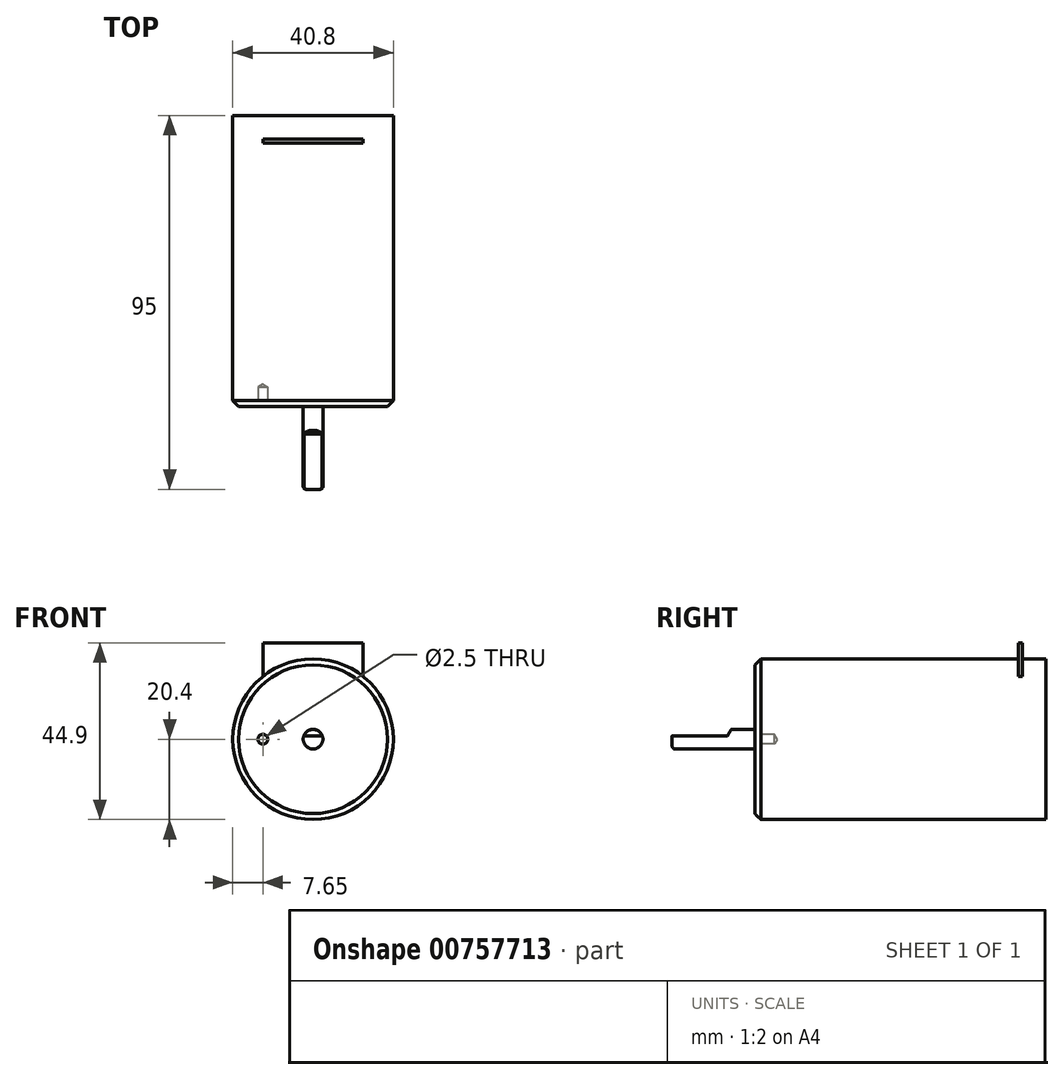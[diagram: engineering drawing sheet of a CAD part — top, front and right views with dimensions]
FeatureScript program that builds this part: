
annotation { "Feature Type Name" : "Feature", "Feature Type Description" : "" }
export const myFeature = defineFeature(function(context is Context, id is Id, definition is map)
    precondition{}
    {
        {
            var Q0;
            Q0=qCreatedBy(makeId("Front.planeOp"),FACE);
            var sketch = newSketch(context, id + "F0", { "sketchPlane" : qUnion([Q0])});
            skCircle(sketch, "E0", {"center": v(0, 0) * mm, "radius": 20.4 * mm});
            skSolve(sketch);
        }
        {
            var Q0;
            Q0 = qSketchRegion(id + "F0", true);
            extrude(context, id + "F1", {"entities" : qUnion([Q0]), "oppositeDirection" : true, "depth" : 74 * mm, "offsetDistance" : 25 * mm});
        }
        {
            var Q0;
            Q0=makeQuery(id+"F1.opExtrude","CAP_EDGE",EDGE,{"disambiguationData":[OSD([sQuery(id+"F0.wireOp",EDGE,"E0")])],"isStart":true});
            chamfer(context, id + "F2", {"entities" : qUnion([Q0]), "width" : 1.5 * mm, "tangentPropagation" : true});
        }
        {
            var Q0;
            Q0=qCreatedBy(makeId("Top.planeOp"),FACE);
            var sketch = newSketch(context, id + "F3", { "sketchPlane" : qUnion([Q0])});
            skLineSegment(sketch, "E1", {"start": v(0, 65.39) * mm, "end": v(0, -94.4) * mm, "construction": true});
            skSolve(sketch);
        }
        {
            var Q0;
            Q0=qCreatedBy(makeId("Front.planeOp"),FACE);
            var sketch = newSketch(context, id + "F4", { "sketchPlane" : qUnion([Q0])});
            skPoint(sketch, "E2", {"position": v(-12.75, 0) * mm});
            skCircle(sketch, "E3", {"center": v(0, 0) * mm, "radius": 12.75 * mm, "construction": true});
            skSolve(sketch);
        }
        {
            var Q0;
            Q0=sQuery(id+"F4.wireOp",VERTEX,"E2");
            var Q1;
            Q1=makeQuery(id+"F1.opExtrude","SWEPT_BODY",BODY,{"disambiguationData":[OSD([sQuery(id+"F0.wireOp",EDGE,"E0")])]});
            hole(context, id + "F5", {"style" : HoleStyle.SIMPLE, "endStyle" : HoleEndStyle.BLIND, "standardTappedOrClearance" : lookupTablePath({ "standard" : "ISO", "engagement" : "75%", "pitch" : "0.5 mm", "size" : "M3", "type" : "Tapped" }), "standardBlindInLast" : lookupTablePath({ "standard" : "ISO", "engagement" : "75%", "pitch" : "0.5 mm", "size" : "M3", "type" : "Tapped" }), "holeDiameter" : 2.5 * mm, "majorDiameter" : 3 * mm, "showTappedDepth" : true, "holeDepth" : 5 * mm, "isTappedThrough" : true, "tappedDepth" : 3.5 * mm, "tapClearance" : 3, "locations" : qUnion([Q0]), "scope" : qUnion([Q1])});
        }
        {
            var Q0;
            Q0=qCreatedBy(makeId("Front.planeOp"),FACE);
            var sketch = newSketch(context, id + "F6", { "sketchPlane" : qUnion([Q0])});
            skCircle(sketch, "E4", {"center": v(0, 0) * mm, "radius": 2.5 * mm});
            skSolve(sketch);
        }
        {
            var Q0;
            Q0=makeQuery(id+"F6.imprint","IMPRINT",FACE,{"disambiguationData":[TD([[makeQuery(id+"F6.imprint","IMPRINT",EDGE,{"derivedFrom":sQuery(id+"F6.wireOp",EDGE,"E4")}),1.0]])]});
            var Q1;
            Q1=sQuery(id+"F6.wireOp",EDGE,"E4");
            extrude(context, id + "F7", {"entities" : qUnion([Q0]), "operationType" : NewBodyOperationType.ADD, "surfaceEntities" : qUnion([Q1]), "depth" : 21 * mm, "offsetDistance" : 25 * mm});
        }
        {
            var Q0;
            Q0=makeQuery(id+"F7.opExtrude","CAP_FACE",FACE,{"disambiguationData":[OSD([sQuery(id+"F6.wireOp",EDGE,"E4")])],"isStart":false});
            var sketch = newSketch(context, id + "F8", { "sketchPlane" : qUnion([Q0])});
            skArc(sketch, "E5.0", {"start": v(2.33, 0.9) * mm, "mid": v(0, 2.5) * mm, "end": v(-2.33, 0.9) * mm});
            skLineSegment(sketch, "E6", {"start": v(-2.33, 0.9) * mm, "end": v(2.33, 0.9) * mm});
            skSolve(sketch);
        }
        {
            var Q0;
            Q0 = qSketchRegion(id + "F8", true);
            extrude(context, id + "F9", {"entities" : qUnion([Q0]), "operationType" : NewBodyOperationType.REMOVE, "oppositeDirection" : true, "depth" : 15 * mm, "offsetDistance" : 25 * mm});
        }
        {
            var Q0;
            Q0=makeQuery(id+"F9.boolean.opBoolean","COPY",EDGE,{"derivedFrom":makeQuery(id+"F9.opExtrude","CAP_EDGE",EDGE,{"disambiguationData":[OSD([sQuery(id+"F8.wireOp",EDGE,"E6")])],"isStart":false})});
            chamfer(context, id + "F10", {"entities" : qUnion([Q0]), "chamferType" : ChamferType.OFFSET_ANGLE, "width" : 1.6 * mm, "oppositeDirection" : false, "angle" : 30 * degree, "tangentPropagation" : true});
        }
        {
            var Q0;
            Q0=makeQuery(id+"F7.opExtrude","CAP_EDGE",EDGE,{"disambiguationData":[OSD([sQuery(id+"F6.wireOp",EDGE,"E4")])],"isStart":false});
            fillet(context, id + "F11", {"entities" : qUnion([Q0]), "radius" : 0.7 * mm, "tangentPropagation" : true, "allowEdgeOverflow" : false});
        }
        {
            var Q0;
            Q0=qCreatedBy(makeId("Front.planeOp"),FACE);
            cPlane(context, id + "F12", {"entities" : qUnion([Q0]), "cplaneType" : CPlaneType.OFFSET, "offset" : 67 * mm, "oppositeDirection" : true, "width" : 150 * mm, "height" : 150 * mm});
        }
        {
            var Q0;
            Q0=qCreatedBy(id+"F12.planeOp",FACE);
            var sketch = newSketch(context, id + "F13", { "sketchPlane" : qUnion([Q0])});
            skLineSegment(sketch, "E7.bottom", {"start": v(12.65, 24.5) * mm, "end": v(-12.65, 24.5) * mm});
            skLineSegment(sketch, "E7.top", {"start": v(12.65, 0) * mm, "end": v(-12.65, 0) * mm});
            skLineSegment(sketch, "E7.left", {"start": v(12.65, 24.5) * mm, "end": v(12.65, 0) * mm});
            skLineSegment(sketch, "E7.right", {"start": v(-12.65, 24.5) * mm, "end": v(-12.65, 0) * mm});
            skLineSegment(sketch, "E8", {"start": v(0, 52.3) * mm, "end": v(0, -34.5) * mm, "construction": true});
            skSolve(sketch);
        }
        {
            var Q0;
            Q0=makeQuery(id+"F13.imprint","IMPRINT",FACE,{"disambiguationData":[TD([[makeQuery(id+"F13.imprint","IMPRINT",EDGE,{"derivedFrom":sQuery(id+"F13.wireOp",EDGE,"E7.bottom")}),1.0]])]});
            extrude(context, id + "F14", {"entities" : qUnion([Q0]), "operationType" : NewBodyOperationType.ADD, "oppositeDirection" : true, "depth" : 1 * mm, "offsetDistance" : 25 * mm});
        }
    });
